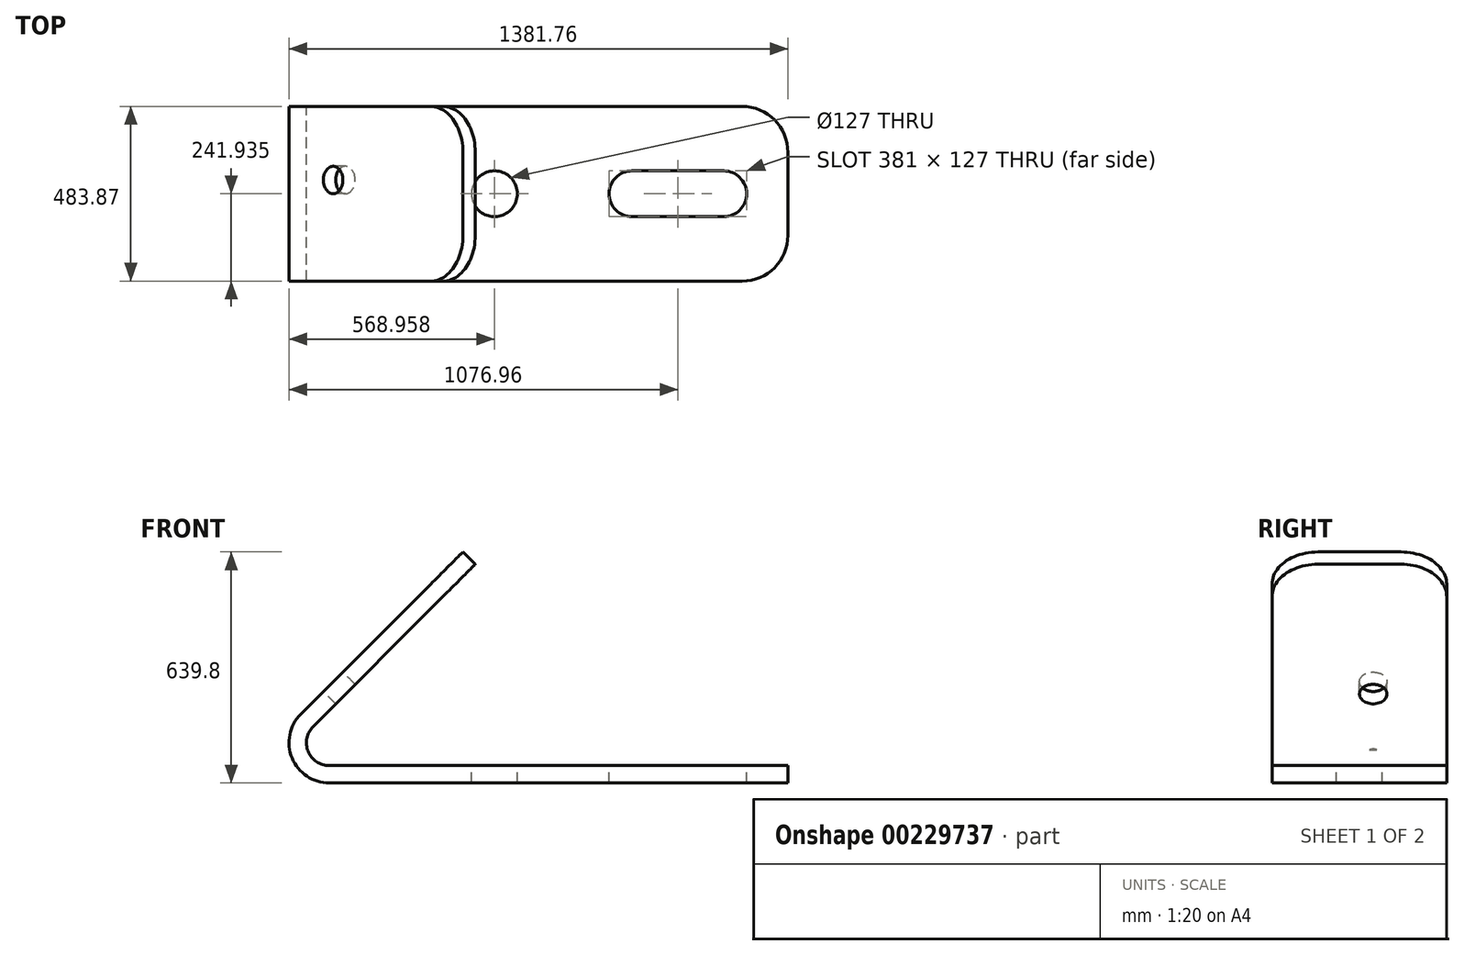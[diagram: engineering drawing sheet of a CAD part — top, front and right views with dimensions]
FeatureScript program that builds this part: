
annotation { "Feature Type Name" : "Feature", "Feature Type Description" : "" }
export const myFeature = defineFeature(function(context is Context, id is Id, definition is map)
    precondition{}
    {
        {
            var Q0;
            Q0=qCreatedBy(makeId("Front.planeOp"),FACE);
            var sketch = newSketch(context, id + "F0", { "sketchPlane" : qUnion([Q0])});
            skLineSegment(sketch, "E0", {"start": v(865.89, 0) * mm, "end": v(-404.11, 0) * mm});
            skLineSegment(sketch, "E1", {"start": v(865.89, 0) * mm, "end": v(865.89, -48.26) * mm});
            skLineSegment(sketch, "E2", {"start": v(865.89, -48.26) * mm, "end": v(-404.11, -48.26) * mm});
            skArc(sketch, "E3", {"start": v(-483.14, 142.53) * mm, "mid": v(-507.36, 20.73) * mm, "end": v(-404.11, -48.26) * mm});
            skLineSegment(sketch, "E4", {"start": v(-483.14, 142.53) * mm, "end": v(-34.12, 591.54) * mm});
            skLineSegment(sketch, "E5", {"start": v(-34.12, 591.54) * mm, "end": v(0, 557.41) * mm});
            skLineSegment(sketch, "E6", {"start": v(0, 557.41) * mm, "end": v(-449.01, 108.4) * mm});
            skArc(sketch, "E7", {"start": v(-449.01, 108.4) * mm, "mid": v(-462.78, 39.2) * mm, "end": v(-404.11, 0) * mm});
            skSolve(sketch);
        }
        {
            var Q0;
            Q0 = qSketchRegion(id + "F0", true);
            extrude(context, id + "F1", {"entities" : qUnion([Q0]), "depth" : 483.87 * mm});
        }
        {
            var Q0;
            Q0=makeQuery(id+"F1.opExtrude","SWEPT_FACE",FACE,{"disambiguationData":[OSD([sQuery(id+"F0.wireOp",EDGE,"E0")])]});
            var sketch = newSketch(context, id + "F2", { "sketchPlane" : qUnion([Q0])});
            skPoint(sketch, "E8.endSnap0", {"position": v(865.89, -241.94) * mm});
            skCircle(sketch, "E9", {"center": v(53.09, -241.94) * mm, "radius": 63.5 * mm});
            skArc(sketch, "E10", {"start": v(434.09, -178.44) * mm, "mid": v(370.59, -241.94) * mm, "end": v(434.09, -305.44) * mm});
            skArc(sketch, "E11", {"start": v(688.09, -305.44) * mm, "mid": v(751.59, -241.94) * mm, "end": v(688.09, -178.44) * mm});
            skLineSegment(sketch, "E12", {"start": v(434.09, -178.44) * mm, "end": v(688.09, -178.44) * mm});
            skLineSegment(sketch, "E13", {"start": v(688.09, -305.44) * mm, "end": v(434.09, -305.44) * mm});
            skPoint(sketch, "E14.end.orphan", {"position": v(751.59, -241.94) * mm});
            skSolve(sketch);
        }
        {
            var Q0;
            Q0 = qSketchRegion(id + "F2", true);
            extrude(context, id + "F3", {"entities" : qUnion([Q0]), "operationType" : NewBodyOperationType.REMOVE, "oppositeDirection" : true, "depth" : 48.26 * mm});
        }
        {
            var Q0;
            Q0=makeQuery(id+"F1.opExtrude","CAP_EDGE",EDGE,{"disambiguationData":[OSD([sQuery(id+"F0.wireOp",EDGE,"E1")])],"isStart":true});
            var Q1;
            Q1=makeQuery(id+"F1.opExtrude","CAP_EDGE",EDGE,{"disambiguationData":[OSD([sQuery(id+"F0.wireOp",EDGE,"E1")])],"isStart":false});
            var Q2;
            Q2=makeQuery(id+"F1.opExtrude","CAP_EDGE",EDGE,{"disambiguationData":[OSD([sQuery(id+"F0.wireOp",EDGE,"E5")])],"isStart":true});
            var Q3;
            Q3=makeQuery(id+"F1.opExtrude","CAP_EDGE",EDGE,{"disambiguationData":[OSD([sQuery(id+"F0.wireOp",EDGE,"E5")])],"isStart":false});
            fillet(context, id + "F4", {"entities" : qUnion([Q0, Q1, Q2, Q3]), "radius" : 127 * mm, "tangentPropagation" : true, "allowEdgeOverflow" : false});
        }
        {
            var Q0;
            Q0=makeQuery(id+"F1.opExtrude","SWEPT_FACE",FACE,{"disambiguationData":[OSD([sQuery(id+"F0.wireOp",EDGE,"E4")])]});
            var sketch = newSketch(context, id + "F5", { "sketchPlane" : qUnion([Q0])});
            skCircle(sketch, "E15", {"center": v(203.65, -114.3) * mm, "radius": 38.1 * mm});
            skCircle(sketch, "E16", {"center": v(203.65, -369.57) * mm, "radius": 38.1 * mm});
            skPoint(sketch, "E17.orphan", {"position": v(203.65, 0) * mm});
            skPoint(sketch, "E18.start.orphan", {"position": v(394.15, -241.94) * mm});
            skSolve(sketch);
        }
        {
            var Q0;
            Q0 = qSketchRegion(id + "F5", true);
            extrude(context, id + "F6", {"entities" : qUnion([Q0]), "operationType" : NewBodyOperationType.REMOVE, "oppositeDirection" : true, "depth" : 48.26 * mm});
        }
    });
